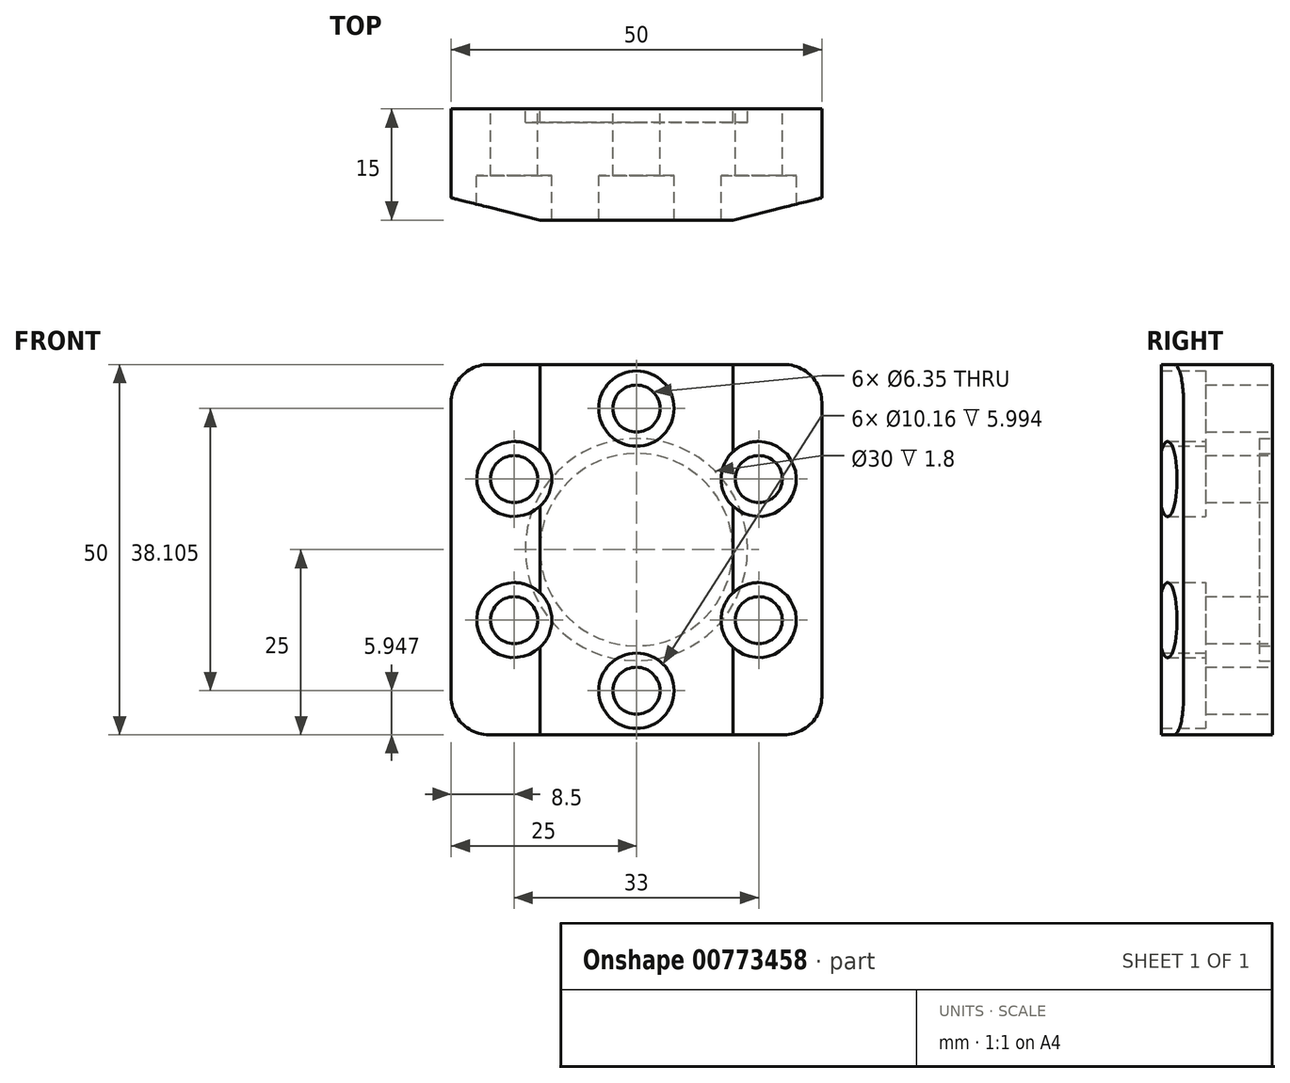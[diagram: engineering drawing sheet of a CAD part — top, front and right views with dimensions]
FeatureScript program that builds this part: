
annotation { "Feature Type Name" : "Feature", "Feature Type Description" : "" }
export const myFeature = defineFeature(function(context is Context, id is Id, definition is map)
    precondition{}
    {
        {
            var Q0;
            Q0=qCreatedBy(makeId("Right.planeOp"),FACE);
            var sketch = newSketch(context, id + "F0", { "sketchPlane" : qUnion([Q0])});
            skLineSegment(sketch, "E0", {"start": v(0, 0) * mm, "end": v(0, 25) * mm});
            skLineSegment(sketch, "E1", {"start": v(0, 0) * mm, "end": v(0, -25) * mm});
            skPoint(sketch, "E2", {"position": v(15, 0) * mm});
            skLineSegment(sketch, "E3", {"start": v(15, 25) * mm, "end": v(15, -25) * mm});
            skLineSegment(sketch, "E4", {"start": v(15, -25) * mm, "end": v(0, -25) * mm});
            skLineSegment(sketch, "E5", {"start": v(0, 25) * mm, "end": v(15, 25) * mm});
            skSolve(sketch);
        }
        {
            var Q0;
            Q0 = qSketchRegion(id + "F0", true);
            extrude(context, id + "F1", {"entities" : qUnion([Q0]), "depth" : 50 * mm, "offsetDistance" : 25.4 * mm});
        }
        {
            var Q0;
            Q0=makeQuery(id+"F1.opExtrude","SWEPT_FACE",FACE,{"disambiguationData":[OSD([sQuery(id+"F0.wireOp",EDGE,"E0"),sQuery(id+"F0.wireOp",EDGE,"E1")])]});
            var sketch = newSketch(context, id + "F2", { "sketchPlane" : qUnion([Q0])});
            skPoint(sketch, "E6", {"position": v(25, 0) * mm});
            skLineSegment(sketch, "E7", {"start": v(25, 0) * mm, "end": v(25, 25) * mm});
            skCircle(sketch, "E8.cCircle", {"center": v(25, 0) * mm, "radius": 16.5 * mm, "construction": true});
            skLineSegment(sketch, "E8.0", {"start": v(8.5, -9.53) * mm, "end": v(8.5, 9.53) * mm});
            skLineSegment(sketch, "E8.1", {"start": v(8.5, 9.53) * mm, "end": v(25, 19.05) * mm});
            skLineSegment(sketch, "E8.2", {"start": v(25, 19.05) * mm, "end": v(41.5, 9.53) * mm});
            skLineSegment(sketch, "E8.3", {"start": v(41.5, 9.53) * mm, "end": v(41.5, -9.53) * mm});
            skLineSegment(sketch, "E8.4", {"start": v(41.5, -9.53) * mm, "end": v(25, -19.05) * mm});
            skLineSegment(sketch, "E8.5", {"start": v(25, -19.05) * mm, "end": v(8.5, -9.53) * mm});
            skPoint(sketch, "E8.0.midPoint", {"position": v(8.5, 0) * mm});
            skCircle(sketch, "E9", {"center": v(25, 19.05) * mm, "radius": 3.1 * mm});
            skCircle(sketch, "E10", {"center": v(41.5, 9.53) * mm, "radius": 3.1 * mm});
            skCircle(sketch, "E11", {"center": v(41.5, -9.53) * mm, "radius": 3.1 * mm});
            skCircle(sketch, "E12", {"center": v(25, -19.05) * mm, "radius": 3.1 * mm});
            skCircle(sketch, "E13", {"center": v(8.5, -9.53) * mm, "radius": 3.1 * mm});
            skCircle(sketch, "E14", {"center": v(8.5, 9.53) * mm, "radius": 3.1 * mm});
            skSolve(sketch);
        }
        {
            var Q0;
            Q0=sQuery(id+"F2.wireOp",VERTEX,"E8.1.end");
            var Q1;
            Q1=sQuery(id+"F2.wireOp",VERTEX,"E8.0.end");
            var Q2;
            Q2=sQuery(id+"F2.wireOp",VERTEX,"E8.2.end");
            var Q3;
            Q3=sQuery(id+"F2.wireOp",VERTEX,"E8.3.end");
            var Q4;
            Q4=sQuery(id+"F2.wireOp",VERTEX,"E8.4.end");
            var Q5;
            Q5=sQuery(id+"F2.wireOp",VERTEX,"E8.0.start");
            var Q6;
            Q6=makeQuery(id+"F1.opExtrude","SWEPT_BODY",BODY,{"disambiguationData":[OSD([sQuery(id+"F0.wireOp",EDGE,"E0"),sQuery(id+"F0.wireOp",EDGE,"E1"),sQuery(id+"F0.wireOp",EDGE,"E3"),sQuery(id+"F0.wireOp",EDGE,"E4"),sQuery(id+"F0.wireOp",EDGE,"E5")])]});
            hole(context, id + "F3", {"style" : HoleStyle.C_BORE, "endStyle" : HoleEndStyle.THROUGH, "holeDiameter" : 6.35 * mm, "cBoreDiameter" : 10.16 * mm, "cBoreDepth" : 6 * mm, "majorDiameter" : 6.35 * mm, "isTappedThrough" : true, "tappedDepth" : 12.7 * mm, "tapClearance" : 3, "locations" : qUnion([Q0, Q1, Q2, Q3, Q4, Q5]), "scope" : qUnion([Q6])});
        }
        {
            var Q0;
            Q0=makeQuery(id+"F1.opExtrude","SWEPT_FACE",FACE,{"disambiguationData":[OSD([sQuery(id+"F0.wireOp",EDGE,"E5")])]});
            var sketch = newSketch(context, id + "F4", { "sketchPlane" : qUnion([Q0])});
            skPoint(sketch, "E15", {"position": v(25, 0) * mm});
            skPoint(sketch, "E16", {"position": v(38, 0) * mm});
            skPoint(sketch, "E17", {"position": v(50, 3) * mm});
            skLineSegment(sketch, "E18", {"start": v(50, 3) * mm, "end": v(38, 0) * mm});
            skPoint(sketch, "E19", {"position": v(12, 0) * mm});
            skPoint(sketch, "E20", {"position": v(0, 3) * mm});
            skLineSegment(sketch, "E21", {"start": v(12, 0) * mm, "end": v(0, 3) * mm});
            skSolve(sketch);
        }
        {
            var Q0;
            Q0 = qSketchRegion(id + "F4", true);
            var Q1;
            {var subQ0=sQuery(id+"F4.wireOp",EDGE,"E18");Q1=makeQuery(id+"F4.imprint","IMPRINT",FACE,{"disambiguationData":[TD([[makeQuery(id+"F4.imprint","IMPRINT",EDGE,{"derivedFrom":subQ0}),1.0]])]});}
            var Q2;
            {var subQ0=sQuery(id+"F4.wireOp",EDGE,"E21");Q2=makeQuery(id+"F4.imprint","IMPRINT",FACE,{"disambiguationData":[TD([[makeQuery(id+"F4.imprint","IMPRINT",EDGE,{"derivedFrom":subQ0}),1.0]])]});}
            extrude(context, id + "F5", {"entities" : qUnion([Q0, Q1, Q2]), "operationType" : NewBodyOperationType.REMOVE, "endBound" : BoundingType.THROUGH_ALL, "oppositeDirection" : true, "depth" : 25.4 * mm, "offsetDistance" : 25.4 * mm});
        }
        {
            var Q0;
            Q0=makeQuery(id+"F1.opExtrude","CAP_EDGE",EDGE,{"disambiguationData":[OSD([sQuery(id+"F0.wireOp",EDGE,"E5")])],"isStart":false});
            var Q1;
            Q1=makeQuery(id+"F1.opExtrude","CAP_EDGE",EDGE,{"disambiguationData":[OSD([sQuery(id+"F0.wireOp",EDGE,"E5")])],"isStart":true});
            var Q2;
            Q2=makeQuery(id+"F1.opExtrude","CAP_EDGE",EDGE,{"disambiguationData":[OSD([sQuery(id+"F0.wireOp",EDGE,"E4")])],"isStart":true});
            var Q3;
            Q3=makeQuery(id+"F1.opExtrude","CAP_EDGE",EDGE,{"disambiguationData":[OSD([sQuery(id+"F0.wireOp",EDGE,"E4")])],"isStart":false});
            fillet(context, id + "F6", {"entities" : qUnion([Q0, Q1, Q2, Q3]), "radius" : 5.08 * mm, "tangentPropagation" : true, "allowEdgeOverflow" : false});
        }
        {
            var Q0;
            Q0=makeQuery(id+"F1.opExtrude","SWEPT_FACE",FACE,{"disambiguationData":[OSD([sQuery(id+"F0.wireOp",EDGE,"E3")])]});
            var sketch = newSketch(context, id + "F7", { "sketchPlane" : qUnion([Q0])});
            skPoint(sketch, "E22", {"position": v(-25, 0) * mm});
            skPoint(sketch, "E22.positionSnap0", {"position": v(-25, 25) * mm});
            skCircle(sketch, "E23", {"center": v(-25, 0) * mm, "radius": 13 * mm});
            skCircle(sketch, "E24", {"center": v(-25, 0) * mm, "radius": 15 * mm});
            skSolve(sketch);
        }
        {
            var Q0;
            Q0=makeQuery(id+"F7.imprint","IMPRINT",FACE,{"disambiguationData":[TD([[makeQuery(id+"F7.imprint","IMPRINT",EDGE,{"derivedFrom":sQuery(id+"F7.wireOp",EDGE,"E23")}),-1.0]])]});
            extrude(context, id + "F8", {"entities" : qUnion([Q0]), "operationType" : NewBodyOperationType.REMOVE, "oppositeDirection" : true, "depth" : 1.8 * mm, "offsetDistance" : 25 * mm});
        }
    });
